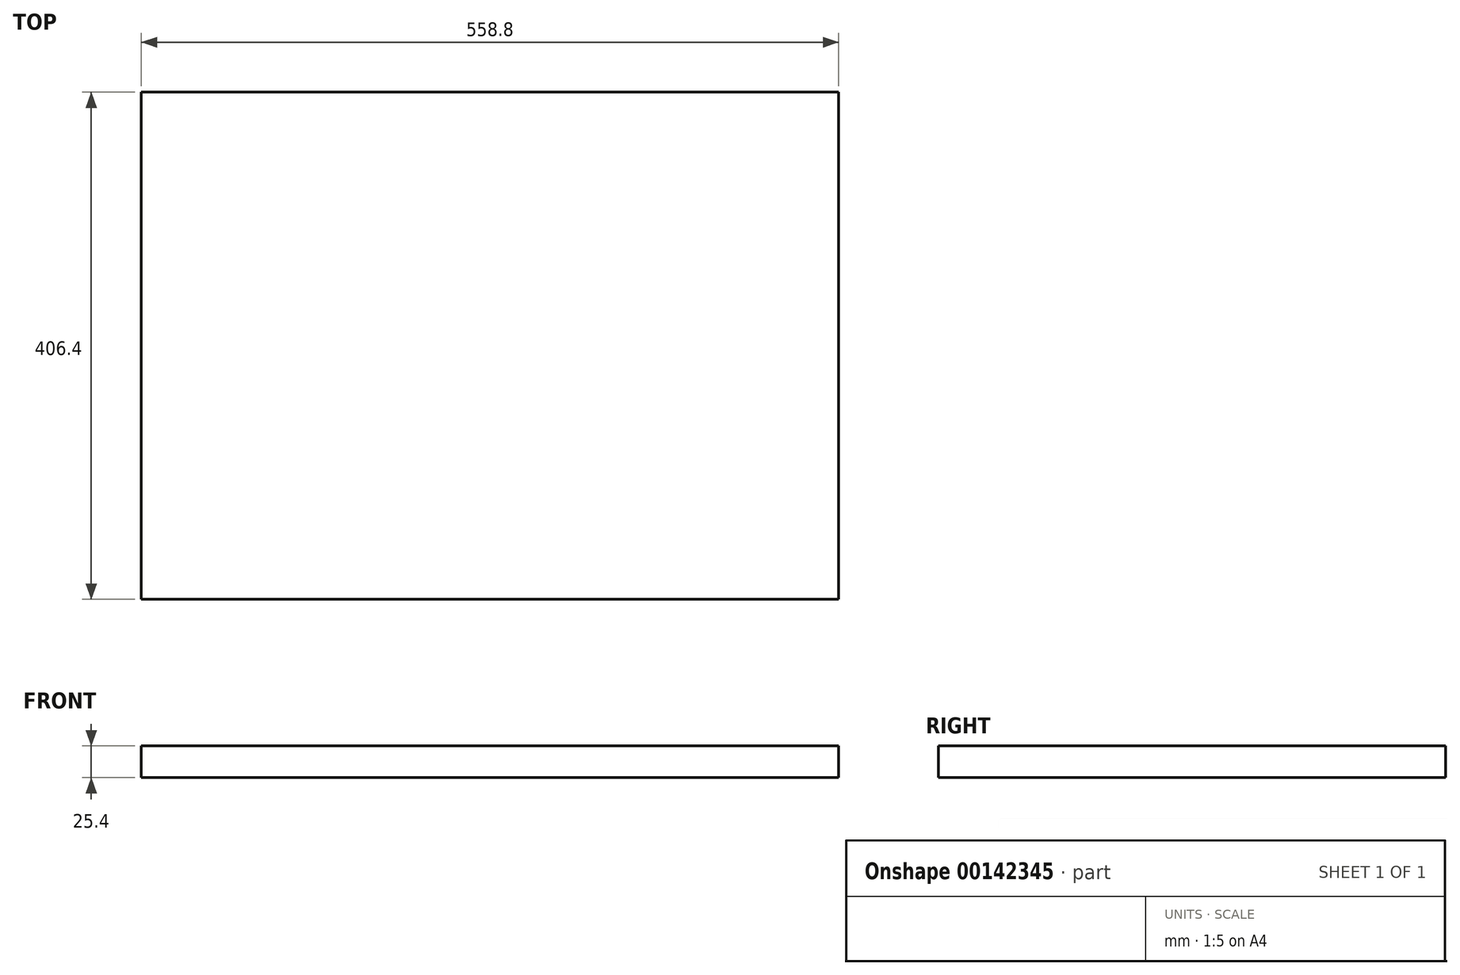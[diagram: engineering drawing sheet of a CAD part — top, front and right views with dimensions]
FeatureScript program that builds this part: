
annotation { "Feature Type Name" : "Feature", "Feature Type Description" : "" }
export const myFeature = defineFeature(function(context is Context, id is Id, definition is map)
    precondition{}
    {
        {
            var Q0;
            Q0=qCreatedBy(makeId("Top.planeOp"),FACE);
            var sketch = newSketch(context, id + "F0", { "sketchPlane" : qUnion([Q0])});
            skLineSegment(sketch, "E0.bottom", {"start": v(-289.68, 203.2) * mm, "end": v(269.12, 203.2) * mm});
            skLineSegment(sketch, "E0.top", {"start": v(-289.68, -203.2) * mm, "end": v(269.12, -203.2) * mm});
            skLineSegment(sketch, "E0.left", {"start": v(-289.68, 203.2) * mm, "end": v(-289.68, -203.2) * mm});
            skLineSegment(sketch, "E0.right", {"start": v(269.12, 203.2) * mm, "end": v(269.12, -203.2) * mm});
            skSolve(sketch);
        }
        {
            var Q0;
            Q0=makeQuery(id+"F0.imprint","IMPRINT",FACE,{"disambiguationData":[TD([[makeQuery(id+"F0.imprint","IMPRINT",EDGE,{"derivedFrom":sQuery(id+"F0.wireOp",EDGE,"E0.bottom")}),-1.0]])]});
            extrude(context, id + "F1", {"entities" : qUnion([Q0]), "depth" : 25.4 * mm});
        }
    });
